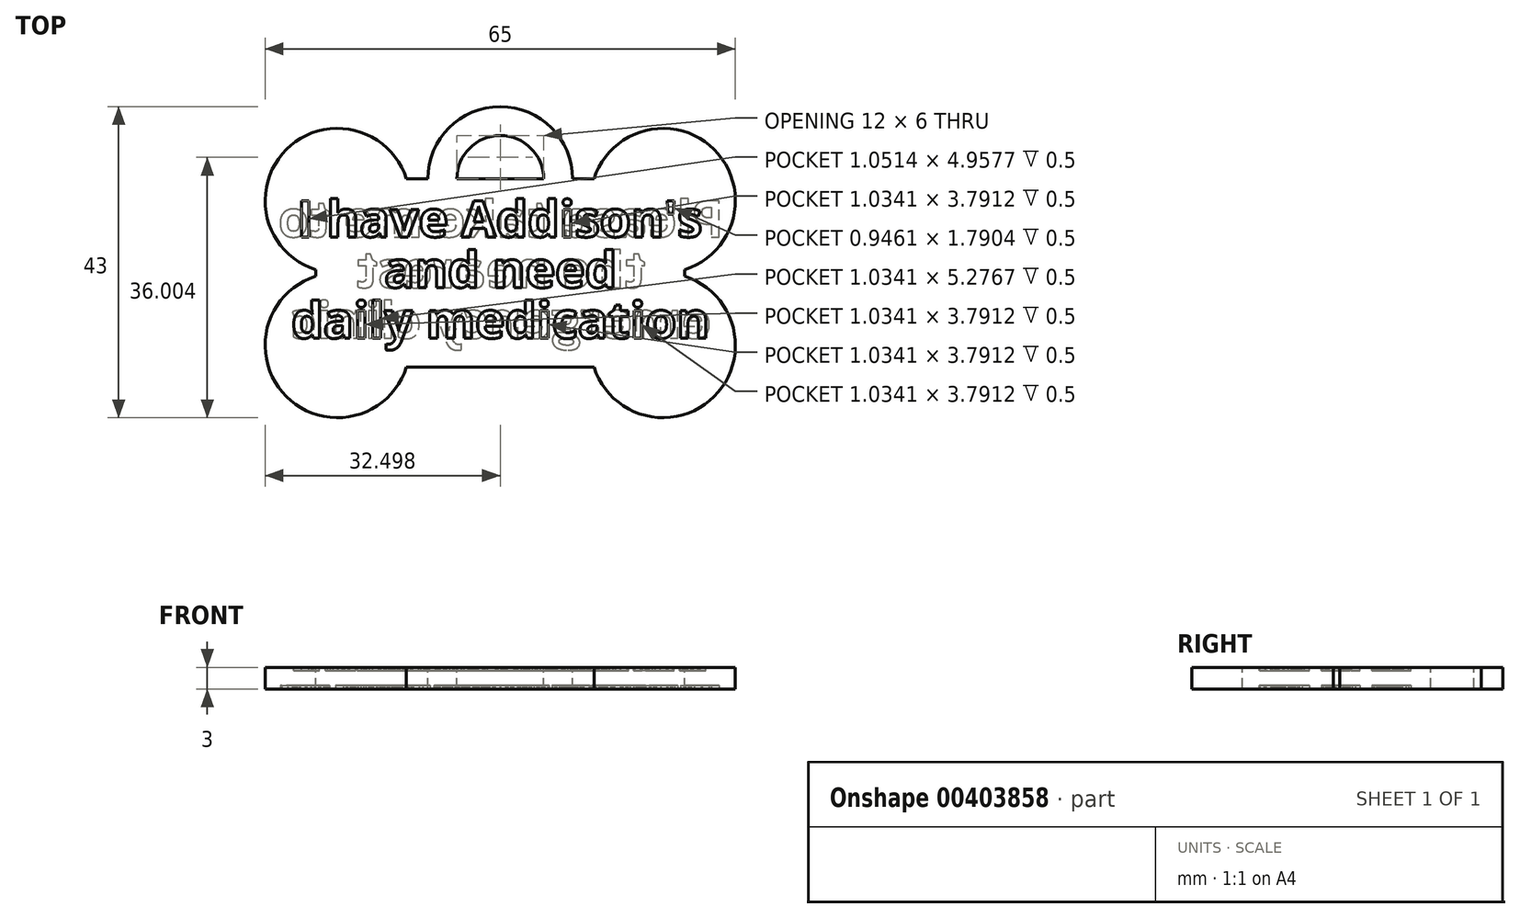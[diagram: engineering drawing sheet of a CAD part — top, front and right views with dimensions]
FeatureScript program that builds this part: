
annotation { "Feature Type Name" : "Feature", "Feature Type Description" : "" }
export const myFeature = defineFeature(function(context is Context, id is Id, definition is map)
    precondition{}
    {
        {
            var Q0;
            Q0=qCreatedBy(makeId("Top.planeOp"),FACE);
            var sketch = newSketch(context, id + "F0", { "sketchPlane" : qUnion([Q0])});
            skLineSegment(sketch, "E0.bottom", {"start": v(-16.01, 14.85) * mm, "end": v(28.99, 14.85) * mm});
            skLineSegment(sketch, "E0.top", {"start": v(-16.01, -5.15) * mm, "end": v(28.99, -5.15) * mm});
            skLineSegment(sketch, "E0.left", {"start": v(-16.01, 14.85) * mm, "end": v(-16.01, -5.15) * mm});
            skLineSegment(sketch, "E0.right", {"start": v(28.99, 14.85) * mm, "end": v(28.99, -5.15) * mm});
            skSolve(sketch);
        }
        {
            var Q0;
            Q0=qSketchRegion(id+"F0",true);
            extrude(context, id + "F1", {"entities" : qUnion([Q0]), "depth" : 3 * mm});
        }
        {
            var Q0;
            Q0=makeQuery(id+"F1.opExtrude","CAP_FACE",FACE,{"disambiguationData":[OSD([sQuery(id+"F0.wireOp",EDGE,"E0.bottom"),sQuery(id+"F0.wireOp",EDGE,"E0.top"),sQuery(id+"F0.wireOp",EDGE,"E0.left"),sQuery(id+"F0.wireOp",EDGE,"E0.right")])],"isStart":false});
            var sketch = newSketch(context, id + "F2", { "sketchPlane" : qUnion([Q0])});
            skCircle(sketch, "E1", {"center": v(28.99, 14.85) * mm, "radius": 10 * mm});
            skCircle(sketch, "E2", {"center": v(28.99, -5.15) * mm, "radius": 10 * mm});
            skCircle(sketch, "E3", {"center": v(-16.01, -5.15) * mm, "radius": 10 * mm});
            skCircle(sketch, "E4", {"center": v(-16.01, 14.85) * mm, "radius": 10 * mm});
            skSolve(sketch);
        }
        {
            var Q0;
            Q0=qSketchRegion(id+"F2",true);
            extrude(context, id + "F3", {"entities" : qUnion([Q0]), "operationType" : NewBodyOperationType.ADD, "oppositeDirection" : true, "depth" : 3 * mm});
        }
        {
            var Q0;
            Q0=makeQuery(id+"F3.boolean.opBoolean","MERGE",FACE,{"derivedFrom":[makeQuery(id+"F1.opExtrude","CAP_FACE",FACE,{"disambiguationData":[OSD([sQuery(id+"F0.wireOp",EDGE,"E0.bottom"),sQuery(id+"F0.wireOp",EDGE,"E0.top"),sQuery(id+"F0.wireOp",EDGE,"E0.left"),sQuery(id+"F0.wireOp",EDGE,"E0.right")])],"isStart":false}),makeQuery(id+"F3.opExtrude","CAP_FACE",FACE,{"disambiguationData":[OSD([sQuery(id+"F2.wireOp",EDGE,"E1")])],"isStart":true}),makeQuery(id+"F3.opExtrude","CAP_FACE",FACE,{"disambiguationData":[OSD([sQuery(id+"F2.wireOp",EDGE,"E2")])],"isStart":true}),makeQuery(id+"F3.opExtrude","CAP_FACE",FACE,{"disambiguationData":[OSD([sQuery(id+"F2.wireOp",EDGE,"E3")])],"isStart":true}),makeQuery(id+"F3.opExtrude","CAP_FACE",FACE,{"disambiguationData":[OSD([sQuery(id+"F2.wireOp",EDGE,"E4")])],"isStart":true})]});
            var sketch = newSketch(context, id + "F4", { "sketchPlane" : qUnion([Q0])});
            skLineSegment(sketch, "E5.bottom", {"start": v(-19.01, 17.85) * mm, "end": v(31.99, 17.85) * mm});
            skLineSegment(sketch, "E5.top", {"start": v(-19.01, -8.15) * mm, "end": v(31.99, -8.15) * mm});
            skLineSegment(sketch, "E5.left", {"start": v(-19.01, 17.85) * mm, "end": v(-19.01, -8.15) * mm});
            skLineSegment(sketch, "E5.right", {"start": v(31.99, 17.85) * mm, "end": v(31.99, -8.15) * mm});
            skSolve(sketch);
        }
        {
            var Q0;
            Q0=qSketchRegion(id+"F4",true);
            extrude(context, id + "F5", {"entities" : qUnion([Q0]), "operationType" : NewBodyOperationType.ADD, "oppositeDirection" : true, "depth" : 3 * mm});
        }
        {
            var Q0;
            {var subQ5=makeQuery(id+"F1.opExtrude","CAP_EDGE",EDGE,{"disambiguationData":[OSD([sQuery(id+"F0.wireOp",EDGE,"E0.bottom")])],"isStart":false});Q0=makeQuery(id+"F4.imprint","IMPRINT",FACE,{"disambiguationData":[TD([[makeQuery(id+"F4.imprint","IMPRINT",EDGE,{"derivedFrom":subQ5}),1.0]])]});}
            var sketch = newSketch(context, id + "F6", { "sketchPlane" : qUnion([Q0])});
            skCircle(sketch, "E6", {"center": v(6.49, 17.85) * mm, "radius": 10 * mm});
            skCircle(sketch, "E7", {"center": v(6.49, 17.85) * mm, "radius": 6 * mm});
            skSolve(sketch);
        }
        {
            var Q0;
            Q0=qSketchRegion(id+"F6",true);
            var Q1;
            Q1=qConstructionFilter(qBodyType(qCreatedBy(id+"F6",EDGE),BodyType.WIRE),ConstructionObject.NO);
            extrude(context, id + "F7", {"entities" : qUnion([Q0]), "operationType" : NewBodyOperationType.ADD, "surfaceEntities" : qUnion([Q1]), "oppositeDirection" : true, "depth" : 3 * mm});
        }
        {
            var Q0;
            Q0=makeQuery(id+"F5.boolean.opBoolean","MERGE",FACE,{"derivedFrom":[makeQuery(id+"F3.boolean.opBoolean","MERGE",FACE,{"derivedFrom":[makeQuery(id+"F1.opExtrude","CAP_FACE",FACE,{"disambiguationData":[OSD([sQuery(id+"F0.wireOp",EDGE,"E0.bottom"),sQuery(id+"F0.wireOp",EDGE,"E0.top"),sQuery(id+"F0.wireOp",EDGE,"E0.left"),sQuery(id+"F0.wireOp",EDGE,"E0.right")])],"isStart":false}),makeQuery(id+"F3.opExtrude","CAP_FACE",FACE,{"disambiguationData":[OSD([sQuery(id+"F2.wireOp",EDGE,"E1")])],"isStart":true}),makeQuery(id+"F3.opExtrude","CAP_FACE",FACE,{"disambiguationData":[OSD([sQuery(id+"F2.wireOp",EDGE,"E2")])],"isStart":true}),makeQuery(id+"F3.opExtrude","CAP_FACE",FACE,{"disambiguationData":[OSD([sQuery(id+"F2.wireOp",EDGE,"E3")])],"isStart":true}),makeQuery(id+"F3.opExtrude","CAP_FACE",FACE,{"disambiguationData":[OSD([sQuery(id+"F2.wireOp",EDGE,"E4")])],"isStart":true})]}),makeQuery(id+"F5.opExtrude","CAP_FACE",FACE,{"disambiguationData":[OSD([sQuery(id+"F4.wireOp",EDGE,"E5.bottom"),sQuery(id+"F4.wireOp",EDGE,"E5.top"),sQuery(id+"F4.wireOp",EDGE,"E5.left"),sQuery(id+"F4.wireOp",EDGE,"E5.right")])],"isStart":true})]});
            var sketch = newSketch(context, id + "F8", { "sketchPlane" : qUnion([Q0])});
            skText(sketch, "E8", { "text": "I have Addison\'s", "fontName": "OpenSans-Bold.ttf"});
            skText(sketch, "E9", { "text": "and need", "fontName": "OpenSans-Bold.ttf"});
            skPoint(sketch, "E10.firstSnap0", {"position": v(-9.53, 5.35) * mm});
            skText(sketch, "E11", { "text": "daily medication", "fontName": "OpenSans-Bold.ttf"});
            skLineSegment(sketch, "E12", {"start": v(6.49, 17.85) * mm, "end": v(6.49, -8.15) * mm, "construction": true});
            const initialGuessF8  = {"E8": [-0.02162, 0.00985, 1, 0, 0.005], "E9": [-0.00953, 0.00285, 1, 0, 0.005], "E11": [-0.02237, -0.00415, 1, 0, 0.005]};
            skSetInitialGuess(sketch, initialGuessF8);
            skSolve(sketch);
        }
        {
            var Q0;
            Q0=qSketchRegion(id+"F8",true);
            extrude(context, id + "F9", {"entities" : qUnion([Q0]), "operationType" : NewBodyOperationType.REMOVE, "oppositeDirection" : true, "depth" : .5 * mm});
        }
        {
            var Q0;
            Q0=makeQuery(id+"F7.boolean.opBoolean","MERGE",FACE,{"derivedFrom":[makeQuery(id+"F5.boolean.opBoolean","MERGE",FACE,{"derivedFrom":[makeQuery(id+"F3.boolean.opBoolean","MERGE",FACE,{"derivedFrom":[makeQuery(id+"F1.opExtrude","CAP_FACE",FACE,{"disambiguationData":[OSD([sQuery(id+"F0.wireOp",EDGE,"E0.bottom"),sQuery(id+"F0.wireOp",EDGE,"E0.top"),sQuery(id+"F0.wireOp",EDGE,"E0.left"),sQuery(id+"F0.wireOp",EDGE,"E0.right")])],"isStart":true}),makeQuery(id+"F3.opExtrude","CAP_FACE",FACE,{"disambiguationData":[OSD([sQuery(id+"F2.wireOp",EDGE,"E1")])],"isStart":false}),makeQuery(id+"F3.opExtrude","CAP_FACE",FACE,{"disambiguationData":[OSD([sQuery(id+"F2.wireOp",EDGE,"E2")])],"isStart":false}),makeQuery(id+"F3.opExtrude","CAP_FACE",FACE,{"disambiguationData":[OSD([sQuery(id+"F2.wireOp",EDGE,"E3")])],"isStart":false}),makeQuery(id+"F3.opExtrude","CAP_FACE",FACE,{"disambiguationData":[OSD([sQuery(id+"F2.wireOp",EDGE,"E4")])],"isStart":false})]}),makeQuery(id+"F5.opExtrude","CAP_FACE",FACE,{"disambiguationData":[OSD([sQuery(id+"F4.wireOp",EDGE,"E5.bottom"),sQuery(id+"F4.wireOp",EDGE,"E5.top"),sQuery(id+"F4.wireOp",EDGE,"E5.left"),sQuery(id+"F4.wireOp",EDGE,"E5.right")])],"isStart":false})]}),makeQuery(id+"F7.opExtrude","CAP_FACE",FACE,{"disambiguationData":[OSD([sQuery(id+"F6.wireOp",EDGE,"E6"),sQuery(id+"F6.wireOp",EDGE,"E7")])],"isStart":false})]});
            var sketch = newSketch(context, id + "F10", { "sketchPlane" : qUnion([Q0])});
            skText(sketch, "E13", { "text": "Please take me to", "fontName": "OpenSans-Bold.ttf"});
            skText(sketch, "E14", { "text": "the nearest", "fontName": "OpenSans-Bold.ttf"});
            skPoint(sketch, "E15.firstSnap0", {"position": v(26.64, -5.35) * mm});
            skText(sketch, "E16", { "text": "emergency clinic", "fontName": "OpenSans-Bold.ttf"});
            skLineSegment(sketch, "E17", {"start": v(6.49, -17.85) * mm, "end": v(6.49, 8.15) * mm, "construction": true});
            const initialGuessF10  = {"E13": [0.03736, -0.00985, -1, 0, 0.005], "E14": [0.02664, -0.00285, -1, 0, 0.005], "E16": [0.03568, 0.00415, -1, 0, 0.005]};
            skSetInitialGuess(sketch, initialGuessF10);
            skSolve(sketch);
        }
        {
            var Q0;
            Q0 = qSketchRegion(id + "F10", true);
            extrude(context, id + "F11", {"entities" : qUnion([Q0]), "operationType" : NewBodyOperationType.REMOVE, "oppositeDirection" : true, "depth" : 0.5 * mm});
        }
    });
